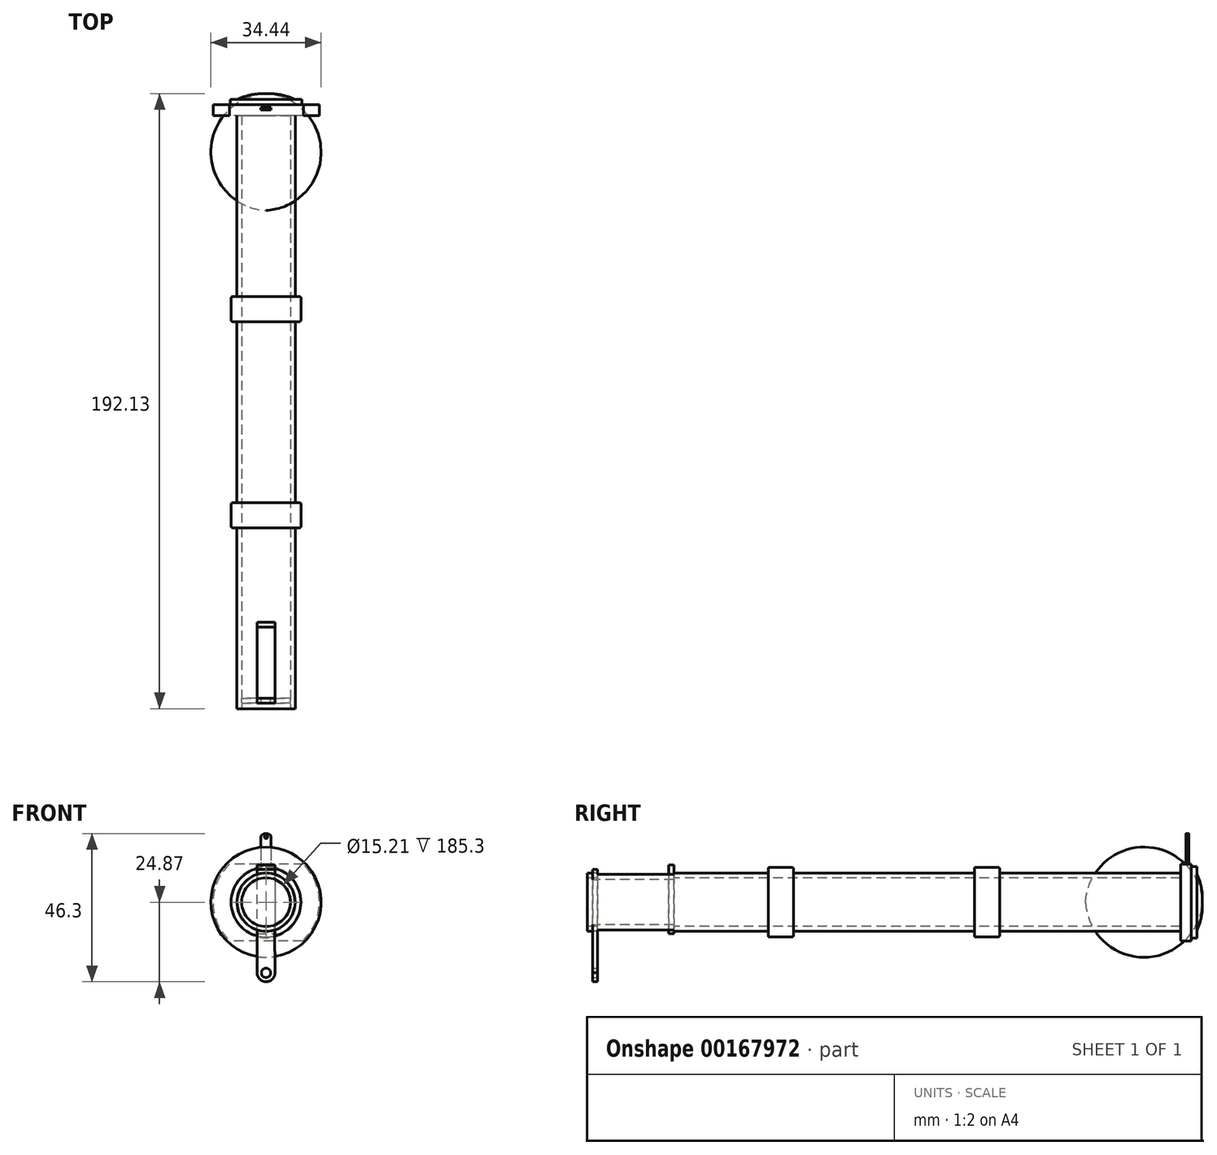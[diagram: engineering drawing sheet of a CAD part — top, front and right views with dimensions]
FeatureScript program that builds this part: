
annotation { "Feature Type Name" : "Feature", "Feature Type Description" : "" }
export const myFeature = defineFeature(function(context is Context, id is Id, definition is map)
    precondition{}
    {
        {
            var Q0;
            Q0=qCreatedBy(makeId("Front.planeOp"),FACE);
            var sketch = newSketch(context, id + "F0", { "sketchPlane" : qUnion([Q0])});
            skCircle(sketch, "E0", {"center": v(0, 0) * mm, "radius": 9.1 * mm});
            skSolve(sketch);
        }
        {
            var Q0;
            Q0=makeQuery(id+"F0.imprint","IMPRINT",FACE,{"disambiguationData":[TD([[makeQuery(id+"F0.imprint","IMPRINT",EDGE,{"derivedFrom":sQuery(id+"F0.wireOp",EDGE,"E0")}),1.0]])]});
            extrude(context, id + "F1", {"entities" : qUnion([Q0]), "depth" : 56.5 * mm});
        }
        {
            var Q0;
            Q0=makeQuery(id+"F1.opExtrude","CAP_FACE",FACE,{"disambiguationData":[OSD([sQuery(id+"F0.wireOp",EDGE,"E0")])],"isStart":true});
            var sketch = newSketch(context, id + "F2", { "sketchPlane" : qUnion([Q0])});
            skLineSegment(sketch, "E1.bottom", {"start": v(-11.44, -12.1) * mm, "end": v(11.44, -12.1) * mm});
            skLineSegment(sketch, "E1.top", {"start": v(-11.64, 11.9) * mm, "end": v(11.44, 11.9) * mm});
            skPoint(sketch, "E1.middle", {"position": v(0, 0) * mm});
            skArc(sketch, "E2", {"start": v(-11.64, 11.9) * mm, "mid": v(-16.65, -0.14) * mm, "end": v(-11.44, -12.1) * mm});
            skArc(sketch, "E3.trimOffspring", {"start": v(11.44, -12.1) * mm, "mid": v(16.55, -0.1) * mm, "end": v(11.44, 11.9) * mm});
            skSolve(sketch);
        }
        {
            var Q0;
            Q0=qSketchRegion(id+"F2",true);
            extrude(context, id + "F3", {"entities" : qUnion([Q0]), "depth" : 1.7 * mm});
        }
        {
            var Q0;
            Q0=makeQuery(id+"F3.opExtrude","CAP_FACE",FACE,{"disambiguationData":[OSD([sQuery(id+"F2.wireOp",EDGE,"E1.bottom"),sQuery(id+"F2.wireOp",EDGE,"E1.top"),sQuery(id+"F2.wireOp",EDGE,"E2"),sQuery(id+"F2.wireOp",EDGE,"E3.trimOffspring")])],"isStart":false});
            extrude(context, id + "F4", {"entities" : qUnion([Q0]), "depth" : 1.7 * mm});
        }
        {
            var Q0;
            Q0=makeQuery(id+"F4.opExtrude","CAP_FACE",FACE,{"disambiguationData":[OSD([sQuery(id+"F2.wireOp",EDGE,"E1.bottom"),sQuery(id+"F2.wireOp",EDGE,"E1.top"),sQuery(id+"F2.wireOp",EDGE,"E2"),sQuery(id+"F2.wireOp",EDGE,"E3.trimOffspring")])],"isStart":false});
            var sketch = newSketch(context, id + "F5", { "sketchPlane" : qUnion([Q0])});
            skCircle(sketch, "E4", {"center": v(0, 0) * mm, "radius": 11.18 * mm});
            skSolve(sketch);
        }
        {
            var Q0;
            Q0=makeQuery(id+"F5.imprint","IMPRINT",FACE,{"disambiguationData":[TD([[makeQuery(id+"F5.imprint","IMPRINT",EDGE,{"derivedFrom":sQuery(id+"F5.wireOp",EDGE,"E4")}),1.0]])]});
            var Q1;
            Q1=sQuery(id+"F5.wireOp",EDGE,"E4");
            extrude(context, id + "F6", {"entities" : qUnion([Q0]), "operationType" : NewBodyOperationType.ADD, "surfaceEntities" : qUnion([Q1]), "depth" : 1.7 * mm});
        }
        {
            var Q0;
            Q0=makeQuery(id+"F1.opExtrude","CAP_FACE",FACE,{"disambiguationData":[OSD([sQuery(id+"F0.wireOp",EDGE,"E0")])],"isStart":false});
            var sketch = newSketch(context, id + "F7", { "sketchPlane" : qUnion([Q0])});
            skCircle(sketch, "E5", {"center": v(0, 0) * mm, "radius": 13.5 * mm});
            skSolve(sketch);
        }
        {
            var Q0;
            Q0=makeQuery(id+"F7.imprint","IMPRINT",FACE,{"disambiguationData":[TD([[makeQuery(id+"F7.imprint","IMPRINT",EDGE,{"derivedFrom":sQuery(id+"F7.wireOp",EDGE,"E5")}),1.0]])]});
            extrude(context, id + "F8", {"entities" : qUnion([Q0]), "depth" : 7.9 * mm});
        }
        {
            var Q0;
            Q0=makeQuery(id+"F8.opExtrude","CAP_FACE",FACE,{"disambiguationData":[OSD([sQuery(id+"F0.wireOp",EDGE,"E0"),sQuery(id+"F7.wireOp",EDGE,"E5")])],"isStart":false});
            var sketch = newSketch(context, id + "F9", { "sketchPlane" : qUnion([Q0])});
            skCircle(sketch, "E6.0", {"center": v(0, 0) * mm, "radius": 9.1 * mm});
            skSolve(sketch);
        }
        {
            var Q0;
            Q0=makeQuery(id+"F9.imprint","IMPRINT",FACE,{"disambiguationData":[TD([[makeQuery(id+"F9.imprint","IMPRINT",EDGE,{"derivedFrom":sQuery(id+"F9.wireOp",EDGE,"E6.0")}),1.0]])]});
            extrude(context, id + "F10", {"entities" : qUnion([Q0]), "depth" : 56.5 * mm});
        }
        {
            var Q0;
            Q0=makeQuery(id+"F10.opExtrude","CAP_FACE",FACE,{"disambiguationData":[OSD([sQuery(id+"F9.wireOp",EDGE,"E6.0")])],"isStart":false});
            var sketch = newSketch(context, id + "F11", { "sketchPlane" : qUnion([Q0])});
            skCircle(sketch, "E7.0", {"center": v(0, 0) * mm, "radius": 9.1 * mm});
            skCircle(sketch, "E8", {"center": v(0, 0) * mm, "radius": 13.5 * mm});
            skSolve(sketch);
        }
        {
            var Q0;
            Q0=makeQuery(id+"F11.imprint","IMPRINT",FACE,{"disambiguationData":[TD([[makeQuery(id+"F11.imprint","IMPRINT",EDGE,{"derivedFrom":sQuery(id+"F11.wireOp",EDGE,"E7.0")}),-1.0]])]});
            extrude(context, id + "F12", {"entities" : qUnion([Q0]), "depth" : 7.9 * mm});
        }
        {
            var Q0;
            Q0=makeQuery(id+"F12.opExtrude","CAP_FACE",FACE,{"disambiguationData":[OSD([sQuery(id+"F11.wireOp",EDGE,"E7.0"),sQuery(id+"F11.wireOp",EDGE,"E8")])],"isStart":false});
            var sketch = newSketch(context, id + "F13", { "sketchPlane" : qUnion([Q0])});
            skCircle(sketch, "E9.0", {"center": v(0, 0) * mm, "radius": 9.1 * mm});
            skSolve(sketch);
        }
        {
            var Q0;
            Q0=makeQuery(id+"F1.opExtrude","CAP_FACE",FACE,{"disambiguationData":[OSD([sQuery(id+"F0.wireOp",EDGE,"E0")])],"isStart":true});
            var sketch = newSketch(context, id + "F14", { "sketchPlane" : qUnion([Q0])});
            skCircle(sketch, "E10", {"center": v(0, 0) * mm, "radius": 10.18 * mm});
            skSolve(sketch);
        }
        {
            var Q0;
            Q0=makeQuery(id+"F13.imprint","IMPRINT",FACE,{"disambiguationData":[TD([[makeQuery(id+"F13.imprint","IMPRINT",EDGE,{"derivedFrom":sQuery(id+"F13.wireOp",EDGE,"E9.0")}),1.0]])]});
            extrude(context, id + "F15", {"entities" : qUnion([Q0]), "depth" : 56.5 * mm});
        }
        {
            var Q0;
            Q0=qCreatedBy(makeId("Right.planeOp"),FACE);
            var sketch = newSketch(context, id + "F16", { "sketchPlane" : qUnion([Q0])});
            skLineSegment(sketch, "E11", {"start": v(-185.3, 9.1) * mm, "end": v(-128.8, 9.1) * mm});
            skLineSegment(sketch, "E12.0", {"start": v(-64.4, 9.1) * mm, "end": v(-64.4, 10.9) * mm});
            skLineSegment(sketch, "E12.1", {"start": v(-56.5, 9.1) * mm, "end": v(-56.5, 10.9) * mm});
            skLineSegment(sketch, "E13.0", {"start": v(0, 10.18) * mm, "end": v(0, -10.18) * mm, "construction": true});
            skLineSegment(sketch, "E14.0", {"start": v(-128.8, 9.1) * mm, "end": v(-128.8, 10.9) * mm});
            skLineSegment(sketch, "E14.1", {"start": v(-120.9, 9.1) * mm, "end": v(-120.9, 10.9) * mm});
            skLineSegment(sketch, "E15", {"start": v(-185.3, 0) * mm, "end": v(-183.8, 0) * mm});
            skLineSegment(sketch, "E16.trimOffspring", {"start": v(-56.5, 9.1) * mm, "end": v(0, 9.1) * mm});
            skLineSegment(sketch, "E17.trimOffspring", {"start": v(-120.9, 9.1) * mm, "end": v(-64.4, 9.1) * mm});
            skLineSegment(sketch, "E18", {"start": v(0, 10.18) * mm, "end": v(0, 9.1) * mm});
            skLineSegment(sketch, "E19", {"start": v(-128.8, 10.9) * mm, "end": v(-120.9, 10.9) * mm});
            skLineSegment(sketch, "E20", {"start": v(-64.4, 10.9) * mm, "end": v(-56.5, 10.9) * mm});
            skLineSegment(sketch, "E21", {"start": v(-185.3, 0) * mm, "end": v(-185.3, 9.1) * mm});
            skLineSegment(sketch, "E22", {"start": v(0, 9.1) * mm, "end": v(0, 0) * mm});
            skLineSegment(sketch, "E23", {"start": v(-185.3, 0) * mm, "end": v(0, 0) * mm, "construction": true});
            skLineSegment(sketch, "E24", {"start": v(-185.3, 7.6) * mm, "end": v(0, 7.6) * mm});
            skLineSegment(sketch, "E25", {"start": v(0, 7.6) * mm, "end": v(0, 9.1) * mm, "construction": true});
            skSolve(sketch);
        }
        {
            var Q0;
            Q0 = qSketchRegion(id + "F16", true);
            var Q1;
            Q1=sQuery(id+"F16.wireOp",EDGE,"E23");
            revolve(context, id + "F17", {"entities" : qUnion([Q0]), "axis" : qUnion([Q1]), "revolveType" : RevolveType.FULL});
        }
        {
            var Q0;
            Q0=makeQuery(id+"F3.opExtrude","CAP_FACE",FACE,{"disambiguationData":[OSD([sQuery(id+"F2.wireOp",EDGE,"E1.bottom"),sQuery(id+"F2.wireOp",EDGE,"E1.top"),sQuery(id+"F2.wireOp",EDGE,"E2"),sQuery(id+"F2.wireOp",EDGE,"E3.trimOffspring")])],"isStart":false});
            var sketch = newSketch(context, id + "F18", { "sketchPlane" : qUnion([Q0])});
            skLineSegment(sketch, "E26.top", {"start": v(-1.59, 11.9) * mm, "end": v(1.59, 11.9) * mm});
            skLineSegment(sketch, "E26.left", {"start": v(-1.59, 20.66) * mm, "end": v(-1.59, 11.9) * mm});
            skLineSegment(sketch, "E26.right", {"start": v(1.59, 21.08) * mm, "end": v(1.59, 11.9) * mm});
            skLineSegment(sketch, "E27", {"start": v(0, 26.8) * mm, "end": v(0, 0) * mm, "construction": true});
            skArc(sketch, "E28", {"start": v(1.59, 20.66) * mm, "mid": v(0, 21.43) * mm, "end": v(-1.59, 20.66) * mm});
            skPoint(sketch, "E29", {"position": v(0, 21.43) * mm});
            skCircle(sketch, "E30", {"center": v(0, 20.39) * mm, "radius": 0.5 * mm});
            skSolve(sketch);
        }
        {
            var Q0;
            {var subQ0=sQuery(id+"F18.wireOp",EDGE,"E26.top");Q0=makeQuery(id+"F18.imprint","IMPRINT",FACE,{"disambiguationData":[TD([[makeQuery(id+"F18.imprint","IMPRINT",EDGE,{"derivedFrom":subQ0}),1.0]])]});}
            extrude(context, id + "F19", {"entities" : qUnion([Q0]), "operationType" : NewBodyOperationType.ADD, "depth" : .85 * mm});
        }
        {
            var Q0;
            Q0=makeQuery(id+"F17.opRevolve","SWEPT_EDGE",EDGE,{"disambiguationData":[OSD([sQuery(id+"F16.wireOp",EDGE,"E12.1"),sQuery(id+"F16.wireOp",EDGE,"ClWl2qCM-FCGR-OkvP-XvV3-z8ARDEnbj7Hy")])]});
            var Q1;
            Q1=makeQuery(id+"F17.opRevolve","SWEPT_EDGE",EDGE,{"disambiguationData":[OSD([sQuery(id+"F16.wireOp",EDGE,"E12.0"),sQuery(id+"F16.wireOp",EDGE,"ClWl2qCM-FCGR-OkvP-XvV3-z8ARDEnbj7Hy")])]});
            var Q2;
            Q2=makeQuery(id+"F17.opRevolve","SWEPT_EDGE",EDGE,{"disambiguationData":[OSD([sQuery(id+"F16.wireOp",EDGE,"E14.1"),sQuery(id+"F16.wireOp",EDGE,"mBpVfSVQ-rQ3H-D8od-ekcF-LCP7MYq0id4N")])]});
            var Q3;
            Q3=makeQuery(id+"F17.opRevolve","SWEPT_EDGE",EDGE,{"disambiguationData":[OSD([sQuery(id+"F16.wireOp",EDGE,"E14.0"),sQuery(id+"F16.wireOp",EDGE,"mBpVfSVQ-rQ3H-D8od-ekcF-LCP7MYq0id4N")])]});
            fillet(context, id + "F20", {"entities" : qUnion([Q0, Q1, Q2, Q3]), "radius" : .5 * mm, "tangentPropagation" : true, "allowEdgeOverflow" : false});
        }
        {
            var Q0;
            Q0=qCreatedBy(makeId("Right.planeOp"),FACE);
            var sketch = newSketch(context, id + "F21", { "sketchPlane" : qUnion([Q0])});
            skLineSegment(sketch, "E31.0", {"start": v(5.1, 8.81) * mm, "end": v(5.1, -11.18) * mm});
            skPoint(sketch, "E32", {"position": v(5.1, 0) * mm});
            skLineSegment(sketch, "E33", {"start": v(5.1, 0) * mm, "end": v(6.8, 0) * mm});
            skArc(sketch, "E34", {"start": v(6.8, 0) * mm, "mid": v(6.5, 4.51) * mm, "end": v(5.1, 8.81) * mm});
            skSolve(sketch);
        }
        {
            var Q0;
            {var subQ2=sQuery(id+"F21.wireOp",EDGE,"E33");Q0=makeQuery(id+"F21.imprint","IMPRINT",FACE,{"disambiguationData":[TD([[makeQuery(id+"F21.imprint","IMPRINT",EDGE,{"derivedFrom":subQ2}),1.0]])]});}
            var Q1;
            Q1=sQuery(id+"F21.wireOp",EDGE,"E33");
            revolve(context, id + "F22", {"operationType" : NewBodyOperationType.ADD, "entities" : qUnion([Q0]), "axis" : qUnion([Q1]), "revolveType" : RevolveType.FULL});
        }
        {
            var Q0;
            Q0=qCreatedBy(makeId("Top.planeOp"),FACE);
            var sketch = newSketch(context, id + "F23", { "sketchPlane" : qUnion([Q0])});
            skLineSegment(sketch, "E35.0", {"start": v(8.8, -185.25) * mm, "end": v(-8.97, -185.25) * mm});
            skLineSegment(sketch, "E36.bottom", {"start": v(-2.77, -158.25) * mm, "end": v(2.77, -158.25) * mm});
            skLineSegment(sketch, "E36.top", {"start": v(-2.77, -182.05) * mm, "end": v(2.77, -182.05) * mm});
            skLineSegment(sketch, "E36.left", {"start": v(-2.77, -158.25) * mm, "end": v(-2.77, -182.05) * mm});
            skLineSegment(sketch, "E36.right", {"start": v(2.77, -158.25) * mm, "end": v(2.77, -182.05) * mm});
            skPoint(sketch, "E36.middle", {"position": v(0, -170.15) * mm});
            skSolve(sketch);
        }
        {
            var Q0;
            Q0=makeQuery(id+"F12.opExtrude","SWEPT_BODY",BODY,{"disambiguationData":[OSD([sQuery(id+"F11.wireOp",EDGE,"E7.0"),sQuery(id+"F11.wireOp",EDGE,"E8")])]});
            deleteBodies(context, id + "F24", {"entities" : qUnion([Q0])});
        }
        {
            var Q0;
            Q0=makeQuery(id+"F8.opExtrude","SWEPT_BODY",BODY,{"disambiguationData":[OSD([sQuery(id+"F0.wireOp",EDGE,"E0"),sQuery(id+"F7.wireOp",EDGE,"E5")])]});
            var Q1;
            Q1=makeQuery(id+"F15.opExtrude","SWEPT_BODY",BODY,{"disambiguationData":[OSD([sQuery(id+"F13.wireOp",EDGE,"E9.0")])]});
            deleteBodies(context, id + "F25", {"entities" : qUnion([Q0, Q1])});
        }
        {
            var Q0;
            Q0=makeQuery(id+"F10.opExtrude","SWEPT_BODY",BODY,{"disambiguationData":[OSD([sQuery(id+"F9.wireOp",EDGE,"E6.0")])]});
            deleteBodies(context, id + "F26", {"entities" : qUnion([Q0])});
        }
        {
            var Q0;
            Q0=makeQuery(id+"F1.opExtrude","SWEPT_BODY",BODY,{"disambiguationData":[OSD([sQuery(id+"F0.wireOp",EDGE,"E0")])]});
            deleteBodies(context, id + "F27", {"entities" : qUnion([Q0])});
        }
        {
            var Q0;
            Q0=makeQuery(id+"F23.imprint","IMPRINT",FACE,{"disambiguationData":[TD([[makeQuery(id+"F23.imprint","IMPRINT",EDGE,{"derivedFrom":sQuery(id+"F23.wireOp",EDGE,"E36.bottom")}),-1.0]])]});
            extrude(context, id + "F28", {"entities" : qUnion([Q0]), "operationType" : NewBodyOperationType.REMOVE, "endBound" : BoundingType.THROUGH_ALL, "oppositeDirection" : true, "depth" : 25 * mm, "hasSecondDirection" : true, "secondDirectionBound" : SecondDirectionBoundingType.THROUGH_ALL, "secondDirectionOppositeDirection" : false, "secondDirectionDepth" : 25 * mm});
        }
        {
            var Q0;
            Q0=makeQuery(id+"F28.boolean.opBoolean","COPY",FACE,{"disambiguationData":[OD(1.0)],"derivedFrom":makeQuery(id+"F28.opExtrude","SWEPT_FACE",FACE,{"disambiguationData":[OSD([sQuery(id+"F23.wireOp",EDGE,"E36.top")])]})});
            var sketch = newSketch(context, id + "F29", { "sketchPlane" : qUnion([Q0])});
            skArc(sketch, "E37.0", {"start": v(-2.77, -8.67) * mm, "mid": v(0, -9.1) * mm, "end": v(2.77, -8.67) * mm, "construction": true});
            skArc(sketch, "E38", {"start": v(-2.75, 7.1) * mm, "mid": v(0, -7.6) * mm, "end": v(2.77, 7.08) * mm});
            skLineSegment(sketch, "E39.top", {"start": v(-2.72, 0) * mm, "end": v(2.82, 0) * mm, "construction": true});
            skPoint(sketch, "E39.middle", {"position": v(0, 10.34) * mm});
            skLineSegment(sketch, "E40.left", {"start": v(2.77, -8.67) * mm, "end": v(2.77, -8.67) * mm});
            skLineSegment(sketch, "E40.right", {"start": v(-2.77, -8.67) * mm, "end": v(-2.77, -8.67) * mm});
            skLineSegment(sketch, "E41.left", {"start": v(2.77, -8.67) * mm, "end": v(2.75, -10.25) * mm});
            skLineSegment(sketch, "E42", {"start": v(2.82, 0) * mm, "end": v(2.77, -8.67) * mm});
            skLineSegment(sketch, "E43", {"start": v(-2.72, 0) * mm, "end": v(-2.77, -8.67) * mm});
            skLineSegment(sketch, "E44", {"start": v(-2.77, -10.25) * mm, "end": v(-2.77, -8.67) * mm});
            skArc(sketch, "E45.0", {"start": v(2.77, 8.67) * mm, "mid": v(0, 9.1) * mm, "end": v(-2.77, 8.67) * mm, "construction": true});
            skLineSegment(sketch, "E46.MirrorCS", {"start": v(-2.77, -22.3) * mm, "end": v(-2.72, 0) * mm});
            skLineSegment(sketch, "E47.MirrorCS", {"start": v(2.77, -22.09) * mm, "end": v(2.82, 0) * mm});
            skLineSegment(sketch, "E48.MirrorCS", {"start": v(-2.79, -22.09) * mm, "end": v(2.77, -22.09) * mm});
            skArc(sketch, "E49.MirrorCS", {"start": v(2.77, -22.09) * mm, "mid": v(0, -24.87) * mm, "end": v(-2.79, -22.09) * mm});
            skLineSegment(sketch, "E50.MirrorCS", {"start": v(2.75, 10.25) * mm, "end": v(-2.77, 10.25) * mm});
            skLineSegment(sketch, "E51", {"start": v(2.75, 10.25) * mm, "end": v(2.82, 0) * mm});
            skLineSegment(sketch, "E52", {"start": v(-2.77, 10.25) * mm, "end": v(-2.72, 0) * mm});
            skLineSegment(sketch, "E53", {"start": v(0, 10.25) * mm, "end": v(0, -22.09) * mm, "construction": true});
            skCircle(sketch, "E54", {"center": v(0, -22.09) * mm, "radius": 1.46 * mm});
            skSolve(sketch);
        }
        {
            var Q0;
            Q0 = qSketchRegion(id + "F29", true);
            extrude(context, id + "F30", {"entities" : qUnion([Q0]), "oppositeDirection" : true, "depth" : 1.57 * mm});
        }
        {
            var Q0;
            Q0=makeQuery(id+"F28.boolean.opBoolean","COPY",FACE,{"disambiguationData":[OD(1.0)],"derivedFrom":makeQuery(id+"F28.opExtrude","SWEPT_FACE",FACE,{"disambiguationData":[OSD([sQuery(id+"F23.wireOp",EDGE,"E36.bottom")])]})});
            var sketch = newSketch(context, id + "F31", { "sketchPlane" : qUnion([Q0])});
            skLineSegment(sketch, "E55.MirrorCS", {"start": v(-2.77, -9.8) * mm, "end": v(2.77, -9.8) * mm});
            skLineSegment(sketch, "E56", {"start": v(-2.77, -9.8) * mm, "end": v(-2.77, 11.65) * mm});
            skArc(sketch, "E57.0", {"start": v(-1.59, 20.66) * mm, "mid": v(0, 21.43) * mm, "end": v(1.59, 20.66) * mm});
            skLineSegment(sketch, "E57.1", {"start": v(-1.59, 20.66) * mm, "end": v(-1.59, 11.65) * mm});
            skLineSegment(sketch, "E57.2", {"start": v(1.59, 20.66) * mm, "end": v(1.59, 11.65) * mm});
            skCircle(sketch, "E57.3", {"center": v(0, 20.39) * mm, "radius": 0.5 * mm});
            skLineSegment(sketch, "E58", {"start": v(-2.77, 11.65) * mm, "end": v(2.77, 11.65) * mm});
            skLineSegment(sketch, "E59", {"start": v(2.77, 11.65) * mm, "end": v(2.77, -9.8) * mm});
            skPoint(sketch, "E60", {"position": v(0, 11.65) * mm});
            skPoint(sketch, "E61", {"position": v(0, 12.86) * mm});
            skLineSegment(sketch, "E62", {"start": v(0, 11.65) * mm, "end": v(0, 12.86) * mm});
            skPoint(sketch, "E63", {"position": v(0, -9.1) * mm});
            skPoint(sketch, "E63.positionSnap0", {"position": v(0, -9.8) * mm});
            skPoint(sketch, "E64", {"position": v(0, 9.1) * mm});
            skSolve(sketch);
        }
        {
            var Q0;
            Q0=makeQuery(id+"F31.imprint","IMPRINT",FACE,{"disambiguationData":[TD([[makeQuery(id+"F31.imprint","IMPRINT",EDGE,{"derivedFrom":sQuery(id+"F31.wireOp",EDGE,"E57.0")}),-1.0]])]});
            var Q1;
            Q1=makeQuery(id+"F31.imprint","IMPRINT",FACE,{"disambiguationData":[TD([[makeQuery(id+"F31.imprint","IMPRINT",EDGE,{"derivedFrom":sQuery(id+"F31.wireOp",EDGE,"E55.MirrorCS")}),1.0]])]});
            var Q2;
            {var subQ0=sQuery(id+"F23.wireOp",EDGE,"E36.bottom");var subQ1=makeQuery(id+"F28.opExtrude","SWEPT_FACE",FACE,{"disambiguationData":[OSD([subQ0])]});Q2=makeQuery(id+"F31.imprint","IMPRINT",FACE,{"disambiguationData":[TD([[makeQuery(id+"F31.imprint","IMPRINT",EDGE,{"derivedFrom":makeQuery(id+"F28.boolean.opBoolean","INTERSECT",EDGE,{"disambiguationData":[OD(1.0)],"derivedFrom":[makeQuery(id+"F17.opRevolve","SWEPT_FACE",FACE,{"disambiguationData":[OSD([sQuery(id+"F16.wireOp",EDGE,"E11")])]}),subQ1]})}),-1.0]])]});}
            var Q3;
            {var subQ6=makeQuery(id+"F28.boolean.opBoolean","INTERSECT",EDGE,{"disambiguationData":[OD(1.0)],"derivedFrom":[makeQuery(id+"F17.opRevolve","SWEPT_FACE",FACE,{"disambiguationData":[OSD([sQuery(id+"F16.wireOp",EDGE,"E11")])]}),makeQuery(id+"F28.opExtrude","SWEPT_FACE",FACE,{"disambiguationData":[OSD([sQuery(id+"F23.wireOp",EDGE,"E36.bottom")])]})]});Q3=makeQuery(id+"F31.imprint","IMPRINT",FACE,{"disambiguationData":[TD([[makeQuery(id+"F31.imprint","IMPRINT",EDGE,{"derivedFrom":subQ6}),1.0]])]});}
            extrude(context, id + "F32", {"entities" : qUnion([Q0, Q1, Q2, Q3]), "depth" : 1.57 * mm});
        }
    });
